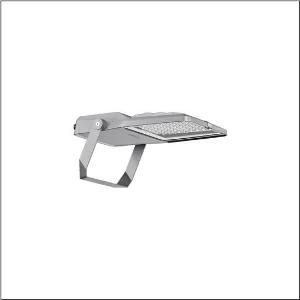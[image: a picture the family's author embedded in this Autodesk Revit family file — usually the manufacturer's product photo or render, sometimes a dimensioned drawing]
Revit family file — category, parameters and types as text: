
# Revit family: floodlight_fl_21_iq_mini___pl64_5xa7772d1e1a_af72
name_source: partatom
category: Lighting Fixtures
units: mm (PartAtom-declared; Revit-internal decimal feet)

## family parameters
Cut with Voids When Loaded = No
Host = Face
Light Source = No
Part Type = Normal
Room Calculation Point = No
Round Connector Dimension = Use Diameter
Shared = No

## types (1)
- --- (1 x LED, 14250 lm, 143 W, 2200K)
    Apparent Load = 143 VA
    CIE Flux Codes = 28 80 98 100 100
    Color Rendering = 70
    Color Temperature = 2200K
    Default Elevation = 1800 mm
    Description = Floodlight FL 21 iQ mini, floodlight, primary light control with lens, of PMMA, primary optical cover: protective disc, of toughened safety glass, transparent, light distribution: PL64, light emission: direct distribution, installation type: surface-mounted, LED, High Power LED, rated luminous flux: 14.250lm, luminous efficacy: 100lm/W, light colour: 722, colour temperature: 2200K, control: Street-Remote, Auto-Match, Temp-Guard, Night-Set, Smart-Wire, Desk-Remote (wireless, voltage-free reading and setting of iQ features in the workshop via application-optimized NFC function/RFID function), optimised constant luminous flux control (CLO 2.0), with terminal, 6-pole, mains connection: 220..240V, AC, 50/60Hz, start of lifetime: 143W, end of service life: 152W, reduction: 61W, luminaire housing, of diecast aluminium, powder-coated, Siteco® metallic grey (DB 702S), corrosivity category C5 mid according to DIN EN ISO 12944, sealing non-destructively replaceable, mounting bracket, of steel, galvanised, powder-coated, Siteco® metallic grey (DB 702S), protection rating (complete): IP66, insulation class (complete): insulation class II (safety insulation), certification: CE, ENEC, VDE, protection symbol: D, impact resistance: IK08, permissible operating ambient temperature: -40..+40°C, permissible operating ambient temperature for outdoor applications: -40..+50°C, standard: DIN EN 12944, LABS conformity tested according to VDMA 24364:2018-05, packaging unit: 1 piece

Light Distribution: PL64
    Height = 70 mm
    Lamp = 1 x LED
    Lamp Light Flux = 14250 lm
    Lamp Power = 143 W
    Lamp count = 1
    Length = 485 mm
    Luminous efficacy = 100 lm/W
    Manufacturer = Siteco
    ModVariant = No
    Model = 5XA7772D1E1A
    Number of Poles = 1
    OnlyDefault = Yes
    Power Factor = 1
    Product Name = Floodlight FL 21 iQ mini | PL64
    Product group = floodlight | pylon annexe
    ProductGroupID = 6200
    Protection Class = Protection class II
    Protection Degree = IP 66
    RLX_Detail_Level = 1
    RLX_Emergency_Light_Flux = 0 lm
    RLX_Emergency_Type = 0
    RLX_Emergency_Type_DB = No
    RlxData = <blob elided: 96569 chars, md5=cd2b3a56>
    Socket = socket
    Standby Power = 0 W
    System Light Flux = 14250 lm
    System Power = 143 W
    Type Comments = factory setting: luminous flux: 100 % | dim-lin: 254 | 730 mA
    Type Image = l_1006845.jpg
    URL = http://relux.com
    VarID = @adj_116067
    Voltage = 0 V
    Weight = 0.00 kg
    Width = 337 mm

## geometry (parser evidence)
native form markers: Blend x4, Sweep x12
no freeform markers — native parametric forms only
